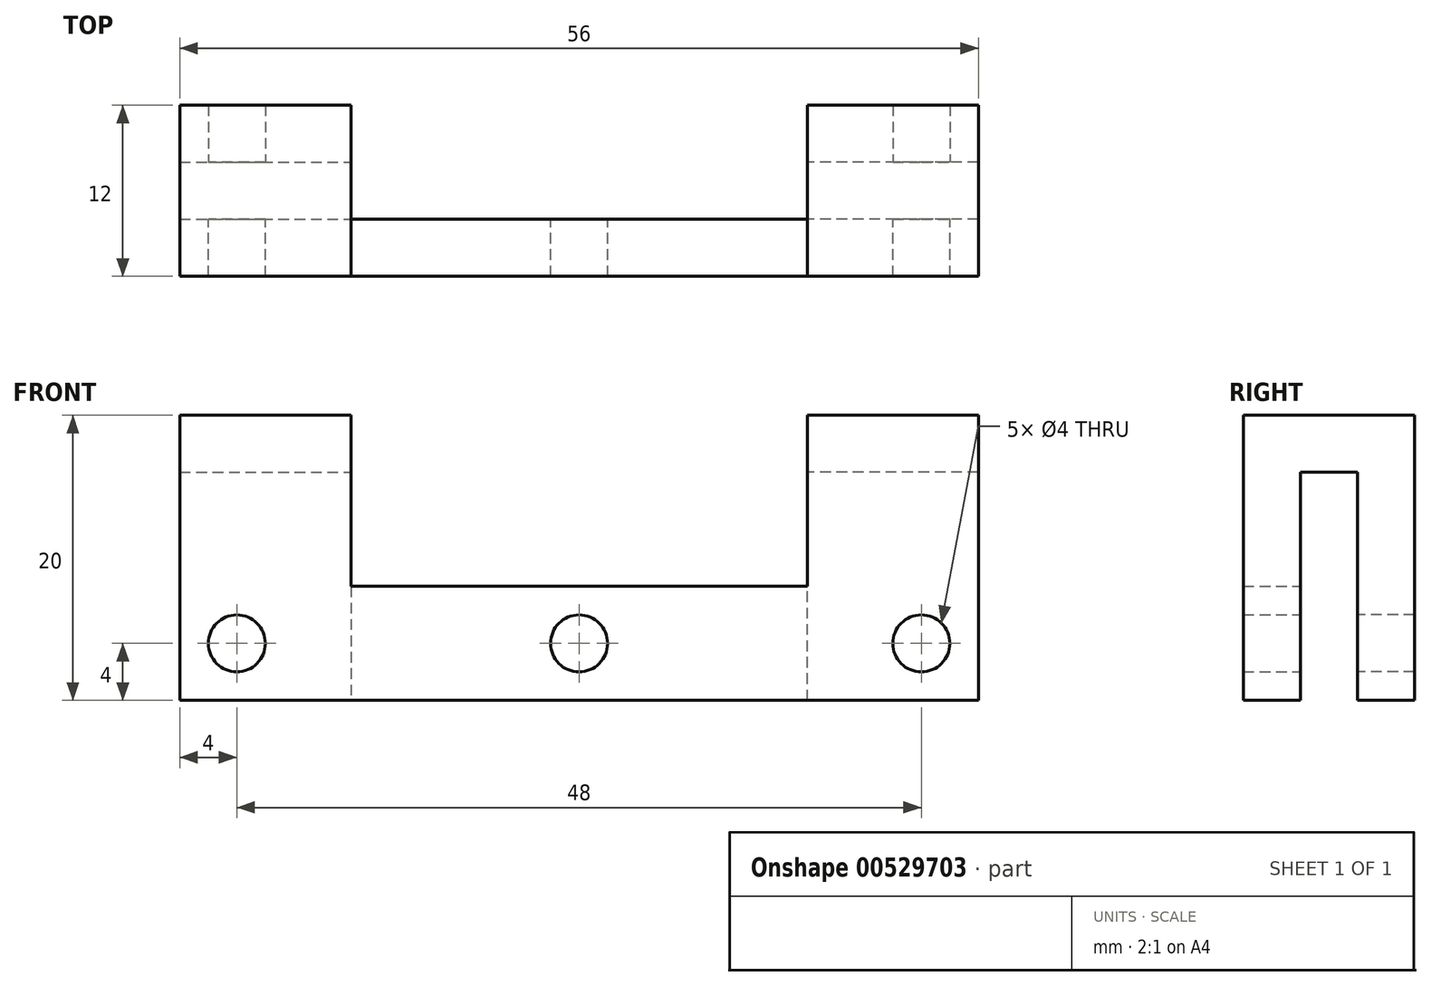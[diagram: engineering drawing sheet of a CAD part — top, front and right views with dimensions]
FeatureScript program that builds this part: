
annotation { "Feature Type Name" : "Feature", "Feature Type Description" : "" }
export const myFeature = defineFeature(function(context is Context, id is Id, definition is map)
    precondition{}
    {
        {
            var Q0;
            Q0=qCreatedBy(makeId("Front.planeOp"),FACE);
            var sketch = newSketch(context, id + "F0", { "sketchPlane" : qUnion([Q0])});
            skLineSegment(sketch, "E0.bottom", {"start": v(28, -4) * mm, "end": v(-28, -4) * mm});
            skLineSegment(sketch, "E0.top", {"start": v(16, 4) * mm, "end": v(-16, 4) * mm});
            skLineSegment(sketch, "E0.left", {"start": v(28, -4) * mm, "end": v(28, 4) * mm});
            skLineSegment(sketch, "E0.right", {"start": v(-28, -4) * mm, "end": v(-28, 4) * mm});
            skPoint(sketch, "E0.middle", {"position": v(0, 0) * mm});
            skCircle(sketch, "E1", {"center": v(-24, 0) * mm, "radius": 2 * mm});
            skCircle(sketch, "E2.MirrorC", {"center": v(24, 0) * mm, "radius": 2 * mm});
            skLineSegment(sketch, "E3.top", {"start": v(28, 16) * mm, "end": v(16, 16) * mm});
            skLineSegment(sketch, "E3.left", {"start": v(28, 4) * mm, "end": v(28, 16) * mm});
            skLineSegment(sketch, "E3.right", {"start": v(16, 4) * mm, "end": v(16, 16) * mm});
            skLineSegment(sketch, "E4.MirrorCS", {"start": v(-28, 4) * mm, "end": v(-28, 16) * mm});
            skLineSegment(sketch, "E5.MirrorCS", {"start": v(-16, 4) * mm, "end": v(-16, 16) * mm});
            skLineSegment(sketch, "E6.MirrorCS", {"start": v(-28, 16) * mm, "end": v(-16, 16) * mm});
            skCircle(sketch, "E7", {"center": v(0, 0) * mm, "radius": 2 * mm});
            skSolve(sketch);
        }
        {
            var Q0;
            Q0 = qSketchRegion(id + "F0", true);
            extrude(context, id + "F1", {"entities" : qUnion([Q0]), "depth" : 4 * mm, "offsetDistance" : 25 * mm});
        }
        {
            var Q0;
            Q0=makeQuery(id+"F1.opExtrude","CAP_FACE",FACE,{"disambiguationData":[OSD([sQuery(id+"F0.wireOp",EDGE,"E0.bottom"),sQuery(id+"F0.wireOp",EDGE,"E0.top"),sQuery(id+"F0.wireOp",EDGE,"E0.left"),sQuery(id+"F0.wireOp",EDGE,"E0.right"),sQuery(id+"F0.wireOp",EDGE,"E1"),sQuery(id+"F0.wireOp",EDGE,"E2.MirrorC"),sQuery(id+"F0.wireOp",EDGE,"E3.top"),sQuery(id+"F0.wireOp",EDGE,"E3.left"),sQuery(id+"F0.wireOp",EDGE,"E3.right"),sQuery(id+"F0.wireOp",EDGE,"E4.MirrorCS"),sQuery(id+"F0.wireOp",EDGE,"E5.MirrorCS"),sQuery(id+"F0.wireOp",EDGE,"E6.MirrorCS")])],"isStart":true});
            var sketch = newSketch(context, id + "F2", { "sketchPlane" : qUnion([Q0])});
            skLineSegment(sketch, "E8.bottom", {"start": v(-28, 16) * mm, "end": v(-16, 16) * mm});
            skLineSegment(sketch, "E8.top", {"start": v(-28, 12) * mm, "end": v(-16, 12) * mm});
            skLineSegment(sketch, "E8.left", {"start": v(-28, 16) * mm, "end": v(-28, 12) * mm});
            skLineSegment(sketch, "E8.right", {"start": v(-16, 16) * mm, "end": v(-16, 12) * mm});
            skLineSegment(sketch, "E9.MirrorCS", {"start": v(16, 16) * mm, "end": v(16, 12) * mm});
            skLineSegment(sketch, "E10.MirrorCS", {"start": v(28, 16) * mm, "end": v(28, 12) * mm});
            skLineSegment(sketch, "E11.MirrorCS", {"start": v(28, 12) * mm, "end": v(16, 12) * mm});
            skLineSegment(sketch, "E12.MirrorCS", {"start": v(28, 16) * mm, "end": v(16, 16) * mm});
            skSolve(sketch);
        }
        {
            var Q0;
            Q0 = qSketchRegion(id + "F2", true);
            extrude(context, id + "F3", {"entities" : qUnion([Q0]), "operationType" : NewBodyOperationType.ADD, "depth" : 4 * mm, "offsetDistance" : 25 * mm});
        }
        {
            var Q0;
            Q0=makeQuery(id+"F3.opExtrude","CAP_FACE",FACE,{"disambiguationData":[OSD([sQuery(id+"F2.wireOp",EDGE,"E8.bottom"),sQuery(id+"F2.wireOp",EDGE,"E8.top"),sQuery(id+"F2.wireOp",EDGE,"E8.left"),sQuery(id+"F2.wireOp",EDGE,"E8.right")])],"isStart":false});
            var sketch = newSketch(context, id + "F4", { "sketchPlane" : qUnion([Q0])});
            skCircle(sketch, "E13", {"center": v(-24, 0) * mm, "radius": 2 * mm});
            skLineSegment(sketch, "E14.bottom", {"start": v(-16, 16) * mm, "end": v(-28, 16) * mm});
            skLineSegment(sketch, "E14.top", {"start": v(-16, -4) * mm, "end": v(-28, -4) * mm});
            skLineSegment(sketch, "E14.left", {"start": v(-16, 16) * mm, "end": v(-16, -4) * mm});
            skLineSegment(sketch, "E14.right", {"start": v(-28, 16) * mm, "end": v(-28, -4) * mm});
            skLineSegment(sketch, "E15.MirrorCS", {"start": v(16, 16) * mm, "end": v(16, -4) * mm});
            skLineSegment(sketch, "E16.MirrorCS", {"start": v(16, 16) * mm, "end": v(28, 16) * mm});
            skCircle(sketch, "E17.MirrorC", {"center": v(24, 0) * mm, "radius": 2 * mm});
            skLineSegment(sketch, "E18.MirrorCS", {"start": v(28, 16) * mm, "end": v(28, -4) * mm});
            skLineSegment(sketch, "E19.MirrorCS", {"start": v(16, -4) * mm, "end": v(28, -4) * mm});
            skSolve(sketch);
        }
        {
            var Q0;
            Q0 = qSketchRegion(id + "F4", true);
            extrude(context, id + "F5", {"entities" : qUnion([Q0]), "operationType" : NewBodyOperationType.ADD, "depth" : 4 * mm, "offsetDistance" : 25 * mm});
        }
    });
